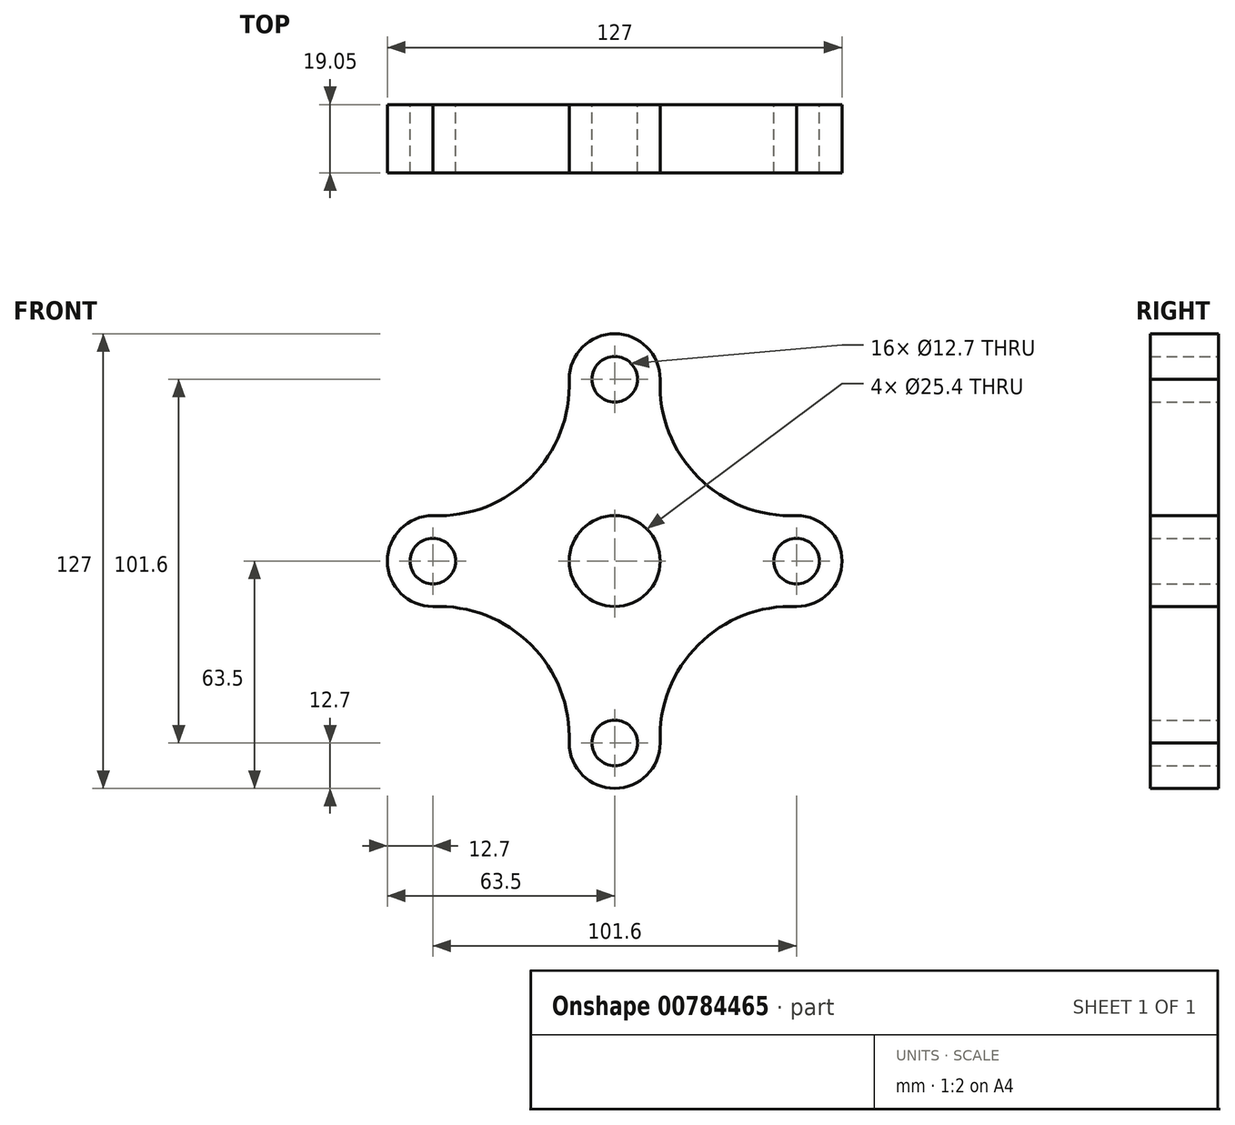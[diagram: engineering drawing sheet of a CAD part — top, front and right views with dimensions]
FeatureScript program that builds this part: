
annotation { "Feature Type Name" : "Feature", "Feature Type Description" : "" }
export const myFeature = defineFeature(function(context is Context, id is Id, definition is map)
    precondition{}
    {
        {
            var Q0;
            Q0=qCreatedBy(makeId("Front.planeOp"),FACE);
            var sketch = newSketch(context, id + "F0", { "sketchPlane" : qUnion([Q0])});
            skCircle(sketch, "E0", {"center": v(0, 0) * mm, "radius": 12.7 * mm});
            skCircle(sketch, "E1", {"center": v(0, 50.8) * mm, "radius": 6.35 * mm});
            skCircle(sketch, "E2.1.0", {"center": v(-50.8, 0) * mm, "radius": 6.35 * mm});
            skCircle(sketch, "E2.2.0", {"center": v(0, -50.8) * mm, "radius": 6.35 * mm});
            skCircle(sketch, "E2.3.0", {"center": v(50.8, 0) * mm, "radius": 6.35 * mm});
            skArc(sketch, "E3", {"start": v(12.7, 50.8) * mm, "mid": v(0, 63.5) * mm, "end": v(-12.7, 50.8) * mm});
            skArc(sketch, "E4.1.0", {"start": v(-50.8, 12.7) * mm, "mid": v(-63.5, 0) * mm, "end": v(-50.8, -12.7) * mm});
            skArc(sketch, "E4.2.0", {"start": v(-12.7, -50.8) * mm, "mid": v(0, -63.5) * mm, "end": v(12.7, -50.8) * mm});
            skArc(sketch, "E4.3.0", {"start": v(50.8, -12.7) * mm, "mid": v(63.5, 0) * mm, "end": v(50.8, 12.7) * mm});
            skArc(sketch, "E5", {"start": v(-50.8, 12.7) * mm, "mid": v(-23.38, 23.38) * mm, "end": v(-12.7, 50.8) * mm});
            skArc(sketch, "E6.1.0", {"start": v(12.7, 50.8) * mm, "mid": v(23.38, 23.38) * mm, "end": v(50.8, 12.7) * mm});
            skArc(sketch, "E6.2.0", {"start": v(50.8, -12.7) * mm, "mid": v(23.38, -23.38) * mm, "end": v(12.7, -50.8) * mm});
            skArc(sketch, "E7.1.0", {"start": v(-12.7, -50.8) * mm, "mid": v(-23.38, -23.38) * mm, "end": v(-50.8, -12.7) * mm});
            skSolve(sketch);
        }
        {
            var Q0;
            Q0 = qSketchRegion(id + "F0", true);
            extrude(context, id + "F1", {"entities" : qUnion([Q0]), "depth" : 19.05 * mm, "offsetDistance" : 25.4 * mm});
        }
    });
